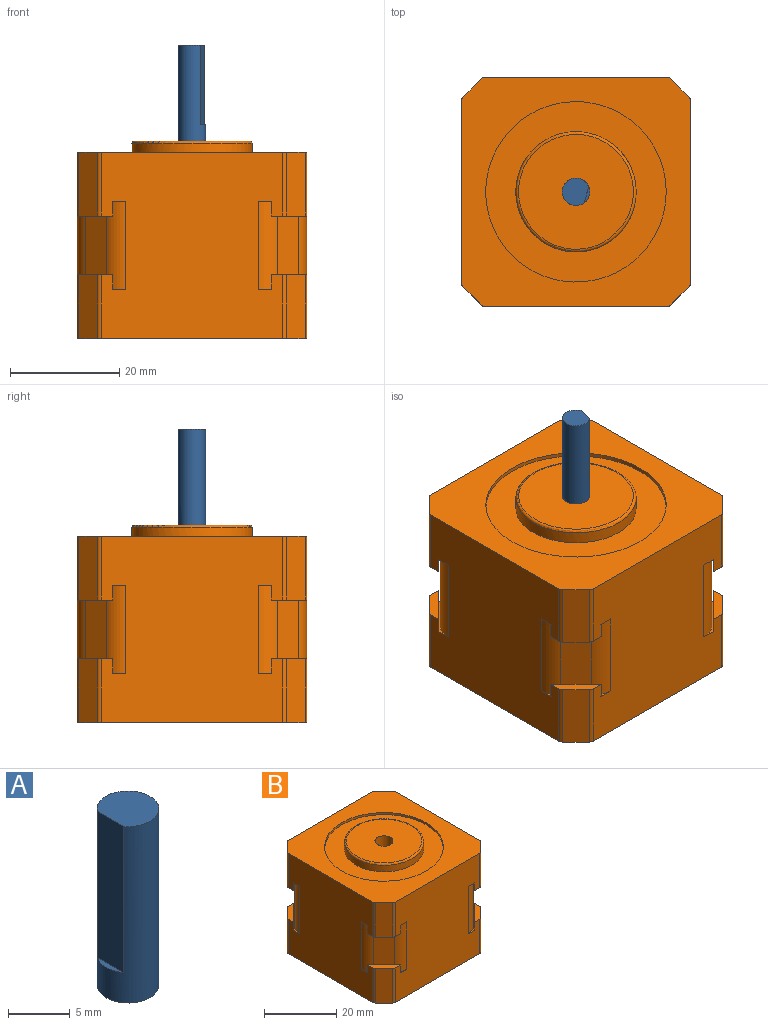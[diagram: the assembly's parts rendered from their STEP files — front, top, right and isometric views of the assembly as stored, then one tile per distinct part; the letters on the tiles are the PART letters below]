
ASSEMBLY  parts=2 mates=1
PART A: 5 faces, bbox 5x5x17.5 mm
  f0: cylinder r=2.5mm len=17.5mm, axis (0,0,-1), area 228.2mm2, adj f1,f2,f3,f4
  f1: plane 14.5x3mm, normal (-1,0,0), area 43.5mm2, adj f0,f2,f4
  f2: plane 5x4.5mm, normal (0,0,1), area 18.6mm2, adj f0,f1
  f3: plane 5x5mm, normal (0,0,-1), area 19.6mm2, adj f0
  f4: plane 3x0.5mm, normal (0,0,1), area 1mm2, adj f0,f1
PART B: 72 faces, bbox 42x42x36.1 mm
  f0: plane 34.1x33.19mm, normal (0,-1,0), area 1008.7mm2, adj f5,f6,f13,f17,f19,f23,f25,f26
  f1: plane 34.1x33.19mm, normal (-1,0,0), area 1008.7mm2, adj f5,f8,f13,f20,f22,f23,f25,f26
  f2: cylinder r=2.5mm len=36.1mm, axis (0,0,-1), area 567.1mm2, adj f13,f70
  f3: plane 34.1x33.19mm, normal (0,1,0), area 1008.7mm2, adj f7,f8,f13,f14,f16,f20,f22,f28
  f4: plane 34.1x33.19mm, normal (1,0,0), area 1008.7mm2, adj f6,f7,f13,f14,f16,f17,f19,f27
  f5: plane 6.5x6.5mm, normal (0,0,1), area 13.1mm2, adj f0,f1,f12,f23,f59,f60
  f6: plane 6.5x6.5mm, normal (0,0,1), area 13.1mm2, adj f0,f4,f9,f17,f61,f62
  f7: plane 6.5x6.5mm, normal (0,0,1), area 13.1mm2, adj f3,f4,f10,f14,f63,f64
  f8: plane 6.5x6.5mm, normal (0,0,1), area 13.1mm2, adj f1,f3,f11,f20,f65,f66
  f9: plane 11.7x3.41mm, normal (0.71,-0.71,0), area 56.4mm2, adj f6,f13,f61,f62
  f10: plane 11.7x3.41mm, normal (0.71,0.71,0), area 56.4mm2, adj f7,f13,f63,f64
  f11: plane 11.7x3.41mm, normal (-0.71,0.71,0), area 56.4mm2, adj f8,f13,f65,f66
  f12: plane 11.7x3.41mm, normal (-0.71,-0.71,0), area 56.4mm2, adj f5,f13,f59,f60
  f13: plane 42x42mm, normal (0,0,-1), area 1712.3mm2, adj f0,f1,f2,f3,f4,f9,f10,f11
  f14: plane 6.5x6.5mm, normal (-0.71,-0.71,0), area 24.8mm2, adj f3,f4,f7,f16
  f15: plane 16.1x3.93mm, normal (0.71,0.71,0), area 89.4mm2, adj f16,f36,f45,f46
  f16: plane 8.93x8.93mm, normal (0,0,1), area 3.4mm2, adj f3,f4,f14,f15,f45,f46
  f17: plane 6.5x6.5mm, normal (-0.71,0.71,0), area 24.8mm2, adj f0,f4,f6,f19
  f18: plane 16.1x3.93mm, normal (0.71,-0.71,0), area 89.4mm2, adj f19,f38,f43,f44
  f19: plane 8.93x8.93mm, normal (0,0,1), area 3.4mm2, adj f0,f4,f17,f18,f43,f44
  f20: plane 6.5x6.5mm, normal (0.71,-0.71,0), area 24.8mm2, adj f1,f3,f8,f22
  f21: plane 16.1x3.93mm, normal (-0.71,0.71,0), area 89.4mm2, adj f22,f40,f47,f48
  f22: plane 8.93x8.93mm, normal (0,0,1), area 3.4mm2, adj f1,f3,f20,f21,f47,f48
  f23: plane 6.5x6.5mm, normal (0.71,0.71,0), area 24.8mm2, adj f0,f1,f5,f25
  f24: plane 16.1x3.93mm, normal (-0.71,-0.71,0), area 89.4mm2, adj f25,f42,f49,f50
  f25: plane 8.93x8.93mm, normal (0,0,1), area 3.4mm2, adj f0,f1,f23,f24,f49,f50
  f26: plane 6.5x6.5mm, normal (0,0,-1), area 13.1mm2, adj f0,f1,f33,f41,f51,f52
  f27: plane 6.5x6.5mm, normal (0,0,-1), area 13.1mm2, adj f0,f4,f30,f37,f53,f54
  f28: plane 6.5x6.5mm, normal (0,0,-1), area 13.1mm2, adj f3,f4,f31,f35,f55,f56
  f29: plane 6.5x6.5mm, normal (0,0,-1), area 13.1mm2, adj f1,f3,f32,f39,f57,f58
  f30: plane 11.7x3.41mm, normal (0.71,-0.71,0), area 56.4mm2, adj f27,f34,f53,f54
  f31: plane 11.7x3.41mm, normal (0.71,0.71,0), area 56.4mm2, adj f28,f34,f55,f56
  f32: plane 11.7x3.41mm, normal (-0.71,0.71,0), area 56.4mm2, adj f29,f34,f57,f58
  f33: plane 11.7x3.41mm, normal (-0.71,-0.71,0), area 56.4mm2, adj f26,f34,f51,f52
  f34: plane 42x42mm, normal (0,0,1), area 876.6mm2, adj f0,f1,f3,f4,f30,f31,f32,f33
  f35: plane 6.5x6.5mm, normal (-0.71,-0.71,0), area 24.8mm2, adj f3,f4,f28,f36
  f36: plane 8.93x8.93mm, normal (0,0,-1), area 3.4mm2, adj f3,f4,f15,f35,f45,f46
  f37: plane 6.5x6.5mm, normal (-0.71,0.71,0), area 24.8mm2, adj f0,f4,f27,f38
  f38: plane 8.93x8.93mm, normal (0,0,-1), area 3.4mm2, adj f0,f4,f18,f37,f43,f44
  f39: plane 6.5x6.5mm, normal (0.71,-0.71,0), area 24.8mm2, adj f1,f3,f29,f40
  f40: plane 8.93x8.93mm, normal (0,0,-1), area 3.4mm2, adj f1,f3,f21,f39,f47,f48
  f41: plane 6.5x6.5mm, normal (0.71,0.71,0), area 24.8mm2, adj f0,f1,f26,f42
  f42: plane 8.93x8.93mm, normal (0,0,-1), area 3.4mm2, adj f0,f1,f24,f41,f49,f50
  f43: cylinder r=5mm len=16.1mm, axis (0,0,-1), area 63.2mm2, adj f4,f18,f19,f38
  f44: cylinder r=5mm len=16.1mm, axis (0,0,1), area 63.2mm2, adj f0,f18,f19,f38
  f45: cylinder r=5mm len=16.1mm, axis (0,0,-1), area 63.2mm2, adj f3,f15,f16,f36
  f46: cylinder r=5mm len=16.1mm, axis (0,0,-1), area 63.2mm2, adj f4,f15,f16,f36
  f47: cylinder r=5mm len=16.1mm, axis (0,0,-1), area 63.2mm2, adj f1,f21,f22,f40
  f48: cylinder r=5mm len=16.1mm, axis (0,0,1), area 63.2mm2, adj f3,f21,f22,f40
  f49: cylinder r=5mm len=16.1mm, axis (0,0,-1), area 63.2mm2, adj f1,f24,f25,f42
  f50: cylinder r=5mm len=16.1mm, axis (0,0,-1), area 63.2mm2, adj f0,f24,f25,f42
  f51: cylinder r=1mm len=11.7mm, axis (0,0,1), area 9.2mm2, adj f1,f26,f33,f34
  f52: cylinder r=1mm len=11.7mm, axis (0,0,1), area 9.2mm2, adj f0,f26,f33,f34
  f53: cylinder r=1mm len=11.7mm, axis (0,0,-1), area 9.2mm2, adj f0,f27,f30,f34
  f54: cylinder r=1mm len=11.7mm, axis (0,0,1), area 9.2mm2, adj f4,f27,f30,f34
  f55: cylinder r=1mm len=11.7mm, axis (0,0,1), area 9.2mm2, adj f4,f28,f31,f34
  f56: cylinder r=1mm len=11.7mm, axis (0,0,1), area 9.2mm2, adj f3,f28,f31,f34
  f57: cylinder r=1mm len=11.7mm, axis (0,0,-1), area 9.2mm2, adj f3,f29,f32,f34
  f58: cylinder r=1mm len=11.7mm, axis (0,0,1), area 9.2mm2, adj f1,f29,f32,f34
  f59: cylinder r=1mm len=11.7mm, axis (0,0,-1), area 9.2mm2, adj f1,f5,f12,f13
  f60: cylinder r=1mm len=11.7mm, axis (0,0,-1), area 9.2mm2, adj f0,f5,f12,f13
  f61: cylinder r=1mm len=11.7mm, axis (0,0,1), area 9.2mm2, adj f0,f6,f9,f13
  f62: cylinder r=1mm len=11.7mm, axis (0,0,-1), area 9.2mm2, adj f4,f6,f9,f13
  f63: cylinder r=1mm len=11.7mm, axis (0,0,-1), area 9.2mm2, adj f4,f7,f10,f13
  f64: cylinder r=1mm len=11.7mm, axis (0,0,-1), area 9.2mm2, adj f3,f7,f10,f13
  f65: cylinder r=1mm len=11.7mm, axis (0,0,1), area 9.2mm2, adj f3,f8,f11,f13
  f66: cylinder r=1mm len=11.7mm, axis (0,0,-1), area 9.2mm2, adj f1,f8,f11,f13
  f67: cylinder r=11mm len=22mm, axis (0,0,1), area 152.1mm2, adj f69,f71
  f68: cylinder r=16.5mm len=33mm, axis (0,0,1), area 72.6mm2, adj f34,f69
  f69: plane 33x33mm, normal (0,0,1), area 475.2mm2, adj f67,f68
  f70: plane 21x21mm, normal (0,0,1), area 326.7mm2, adj f2,f71
  f71: torus R=10.5mm, axis (0,0,-1), area 53.4mm2, adj f67,f70
PLACE A rot(axis=(0,0,1),164.9deg) t=(43.26,22.72,15.66)mm
PLACE B t=(43.26,22.72,-20.44)mm fixed
MATE revolute A.f0 <-> B.f2  axis (0,0,-1) through (43.26,22.72,15.66)mm
